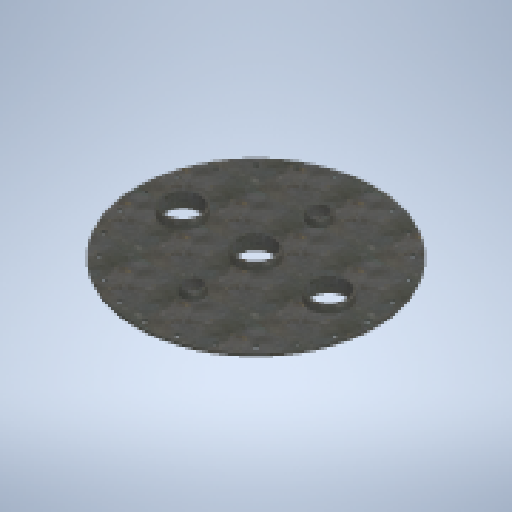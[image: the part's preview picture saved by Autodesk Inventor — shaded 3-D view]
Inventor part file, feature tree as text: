
AUTODESK INVENTOR PART (.ipt)
format: ipt  version: 2023 (Build 270158000, 158)  size: 263,680 bytes
history: native  units: mm
features: extrude x3, sketch x2, pattern_circular x1, projected_geometry x1
ambient origin geometry x8: Origin, YZ Plane, XZ Plane, XY Plane, X Axis, Y Axis, Z Axis, Center Point
bodies: Solid1 (feature_tree)
feature tree (7):
  sketch  "Sketch1"  dims[d0=720.0mm d1=670.0mm]
  extrude  "Extrusion1"  Depth=670.0mm
  extrude  "Extrusion2"  Depth=45.0mm
  pattern_circular  "Circular Pattern1"  [2 undecoded]
  extrude  "Extrusion3"  Depth=45.0mm
  sketch  "Sketch2"  dims[d2=14.2875mm d3=101.6mm d4=101.6mm d5=101.6mm d6=50.8mm d7=50.8mm d8=380.0mm d9=8.0mm d10=0.0mm d11=0.0mm d12=0.0mm d13=240.0mm d14=360.0deg d16=6.0mm d17=8.0mm d18=8.0mm d19=8.0mm d20=6.0mm d21=45.0mm d22=0.0mm d23=440.0mm]
  projected_geometry  "Projected Loop1"
note: 2 required parameter values undecoded (feature->parameter linkage not recoverable at this tier; creation-order binding heuristic only, values carry confidence <= 0.55)
